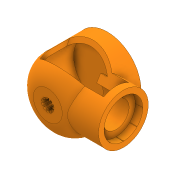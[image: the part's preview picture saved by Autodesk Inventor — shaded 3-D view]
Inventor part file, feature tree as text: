
AUTODESK INVENTOR PART (.ipt)
format: ipt  version: 2020 (Build 240168000, 168)  size: 675,328 bytes
history: native  units: in
note: dims shown in document units (in); Inventor stores cm internally (conversion verified against a paired STEP export)
features: chamfer x32, sketch x19, extrude x18, plane x6, projected_geometry x4, revolve x1
ambient origin geometry x8: Origin, YZ Plane, XZ Plane, XY Plane, X Axis, Y Axis, Z Axis, Center Point
bodies: Solid1 (feature_tree)
feature tree (80):
  extrude  "Extrusion1"  Depth=0.315in TaperAngle=0.0deg
  chamfer  "Chamfer1"  Distance=0.315in
  extrude  "Extrusion2"  Depth=2.3622in TaperAngle=360.0deg
  extrude  "Extrusion3"  Depth=0.315in TaperAngle=0.0deg
  extrude  "Extrusion4"  Depth=0.1575in TaperAngle=0.0deg
  extrude  "Extrusion5"  Depth=0.1575in TaperAngle=0.0deg
  revolve  "Revolution1"  [1 undecoded]
  plane  "Work Plane1"
  extrude  "Extrusion6"  Depth=0.1575in
  plane  "Work Plane2"
  plane  "Work Plane3"
  extrude  "Extrusion8"  [1 undecoded]
  extrude  "Extrusion9"  Depth=0.1575in TaperAngle=0.0deg
  chamfer  "Chamfer3"  Distance=1.8898in
  extrude  "Extrusion10"  Depth=1.2795in
  plane  "Work Plane4"
  extrude  "Extrusion11"  Depth=0.315in TaperAngle=0.0deg
  extrude  "Extrusion12"  Depth=1.1811in
  extrude  "Extrusion13"  Depth=3.1496in TaperAngle=360.0deg
  chamfer  "Chamfer4"  Distance=0.2756in
  chamfer  "Chamfer5"  Distance=0.9843in
  chamfer  "Chamfer6"  Distance=0.315in
  chamfer  "Chamfer7"  Distance=3.937in Angle=360.0deg
  chamfer  "Chamfer8"  Distance=0.315in
  chamfer  "Chamfer9"  Distance=0.315in
  chamfer  "Chamfer10"  Distance=0.315in
  chamfer  "Chamfer11"  Distance=0.315in
  chamfer  "Chamfer12"  Distance=0.315in
  chamfer  "Chamfer13"  Distance=0.315in
  chamfer  "Chamfer14"  Distance=0.315in
  chamfer  "Chamfer15"  Distance=0.315in
  chamfer  "Chamfer16"  Distance=0.315in
  chamfer  "Chamfer17"  Distance=0.315in
  chamfer  "Chamfer18"  Distance=0.315in
  chamfer  "Chamfer19"  Distance=0.315in
  chamfer  "Chamfer20"  Distance=0.315in
  chamfer  "Chamfer21"  Distance=0.315in
  chamfer  "Chamfer22"  Distance=0.315in
  chamfer  "Chamfer23"  Distance=0.315in
  chamfer  "Chamfer24"  Distance=0.315in
  chamfer  "Chamfer25"  Distance=0.315in
  chamfer  "Chamfer26"  Distance=0.315in
  chamfer  "Chamfer27"  Distance=0.315in
  chamfer  "Chamfer28"  Distance=0.315in
  chamfer  "Chamfer29"  Distance=0.315in
  chamfer  "Chamfer30"  Distance=0.315in
  chamfer  "Chamfer31"  Distance=0.315in
  chamfer  "Chamfer32"  Distance=0.315in
  chamfer  "Chamfer33"  Distance=0.315in
  plane  "Work Plane5"
  extrude  "Extrusion15"  Depth=0.315in
  extrude  "Extrusion16"  Depth=0.315in
  plane  "Work Plane6"
  extrude  "Extrusion18"  Depth=0.315in
  extrude  "Extrusion20"  Depth=0.315in
  extrude  "Extrusion21"  Depth=0.9843in
  extrude  "Extrusion22"  [1 undecoded]
  sketch  "Sketch1"  dims[d0=0.4724in d1=0.315in d2=0.0in d3=0.315in d4=0.125in d5=0.0137in]
  sketch  "Sketch2"  dims[d6=0.0157in d7=2.3622in d9=360.0deg]
  sketch  "Sketch3"  dims[d11=0.315in d12=0.0in d13=0.0197in d14=0.0in]
  projected_geometry  "Projected Loop1"
  sketch  "Sketch4"  dims[d15=2.5591in d16=0.1575in d17=0.0in]
  sketch  "Sketch5"  dims[d18=0.1575in d19=1.2598in d20=0.0in]
  sketch  "Sketch6"  dims[d21=1.1024in d22=0.5512in]
  sketch  "Sketch7"  dims[d23=0.8465in d24=0.1575in]
  sketch  "Sketch9"  dims[d25=90.0deg d26=-2.1063in]
  sketch  "Sketch10"  dims[d27=0.1575in d28=0.1575in d29=0.0in d33=-0.1575in d41=1.8898in]
  sketch  "Sketch11"  dims[d42=1.2795in d43=1.8898in]
  sketch  "Sketch12"  dims[d44=0.2165in d45=0.315in d46=0.0in]
  sketch  "Sketch13"  dims[d47=1.1811in d48=0.0in d49=0.2756in d50=0.125in d51=0.0137in]
  sketch  "Sketch14"  dims[d52=0.0157in d53=3.1496in d55=360.0deg d57=0.2756in d58=0.0in]
  sketch  "Sketch16"  dims[d59=-0.2756in d61=0.9843in d62=0.0in]
  sketch  "Sketch17"  dims[d63=0.4764in d64=0.315in d65=0.0in]
  sketch  "Sketch19"  dims[d66=0.0787in]
  projected_geometry  "Projected Loop2"
  projected_geometry  "Projected Loop3"
  sketch  "Sketch21"  dims[d67=0.0787in]
  sketch  "Sketch22"  dims[d68=0.0394in d69=3.937in d71=360.0deg d73=0.315in d74=0.0in d75=0.315in d76=0.125in d77=0.0137in d78=0.315in d79=0.125in d80=0.0137in d81=0.315in d82=0.125in d83=0.0137in d84=0.315in d85=0.125in d86=0.0137in d87=0.315in d88=0.125in d89=0.0137in d90=0.315in d91=0.125in d92=0.0137in d93=0.315in d94=0.125in d95=0.0137in d96=0.315in d97=0.125in d98=0.0137in d99=0.315in d100=0.125in d101=0.0137in d102=0.315in d103=0.125in d104=0.0137in d105=0.315in d106=0.125in d107=0.0137in d108=0.315in d109=0.125in d110=0.0137in d111=0.315in d112=0.125in d113=0.0137in d114=0.315in d115=0.125in d116=0.0137in d117=0.315in d118=0.125in d119=0.0137in d120=0.315in d121=0.125in d122=0.0137in d123=0.315in d124=0.125in d125=0.0137in d126=0.315in d127=0.125in d128=0.0137in d129=0.315in d130=0.125in d131=0.0137in d132=0.315in d133=0.125in d134=0.0137in d135=0.315in d136=0.125in d137=0.0137in d138=0.315in d139=0.125in d140=0.0137in d141=0.315in d142=0.125in d143=0.0137in d144=0.315in d145=0.125in d146=0.0137in d147=0.315in d148=0.125in d149=0.0137in]
  sketch  "Sketch23"  dims[d150=0.315in d151=0.125in d152=0.0137in d153=0.315in d154=0.125in d155=0.0137in d156=0.315in d157=0.125in d158=0.0137in d159=0.315in d160=0.125in d161=0.0137in d162=0.315in d163=0.125in d164=0.0137in d166=0.9843in d171=-0.2756in d172=60.0deg d173=60.0deg d174=0.0in d175=0.0in d176=2.3622in d177=0.0in d178=0.315in d179=0.2067in d180=0.0787in d181=45.0deg d182=0.1969in d183=0.0in d187=-0.6693in d188=0.1969in d189=0.0in d193=0.315in d194=0.0984in d195=0.0in d196=0.2362in d197=0.0984in d198=0.0in d199=0.0984in d200=0.0in]
  projected_geometry  "Projected Loop4"
note: 3 required parameter values undecoded (feature->parameter linkage not recoverable at this tier; creation-order binding heuristic only, values carry confidence <= 0.55)